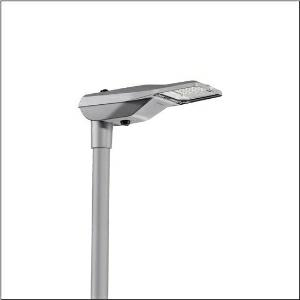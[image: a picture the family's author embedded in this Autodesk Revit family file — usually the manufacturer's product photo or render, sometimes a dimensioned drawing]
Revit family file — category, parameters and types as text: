
# Revit family: streetlight_sl_21_micro___p0_5a_5xe1v33t08db_2423
name_source: partatom
category: Lighting Fixtures
units: mm (PartAtom-declared; Revit-internal decimal feet)

## family parameters
Cut with Voids When Loaded = No
Host = Face
Light Source = No
Part Type = Normal
Room Calculation Point = No
Round Connector Dimension = Use Diameter
Shared = No

## types (1)
- --- (1 x LED, 4940 lm, 39.1 W, 3000K)
    Apparent Load = 39 VA
    CIE Flux Codes = 37 73 96 100 100
    Color Rendering = 70
    Color Temperature = 3000K
    Default Elevation = 1800 mm
    Description = Streetlight SL 21 micro, mast luminaire, primary light control with lens, of PMMA, primary optical cover: cover, of toughened safety glass, transparent, light distribution: P0.5a, light emission: direct distribution, primary light characteristic: asymmetric, installation type: post-top, side-entry, LED, High Power LED, rated luminous flux: 4.940lm, luminous efficacy: 126lm/W, light colour: 730, colour temperature: 3000K, control gear: D4i, control: pre-setting: logarithmic dimming characteristic, flexible luminous flux parameterisation, time-dependent luminous flux control, constant luminous flux control, overheat protection, mains connection: 220..240V, AC, 50/60Hz, start of lifetime: 39W, end of service life: 41W, reduction: 18W, luminaire housing, of diecast aluminium, powder-coated, SITECO metallic grey (DB 702S), corrosivity category C5 high according to DIN EN ISO 12944, multi-level sealing system, sealing non-destructively replaceable, inclination adjustable: 0°, 5°, 10°, 15°, please order mast flange separately, length: 528mm, width: 235mm, height: 110mm, mast flange for spigot size: 42mm (side-entry): 5XC10008XM4, 60/48mm (side-entry/post-top): 5XC10108XM2, 76/60mm (side-entry/post-top): 5XC10108XM1, Smart Interface below and above, protection rating (complete): IP66, insulation class (complete): insulation class II (safety insulation), certification: CE, ENEC, ENEC+, VDE, impact resistance: IK10, permissible operating ambient temperature for outdoor applications: -40..+50°C, standard-compliant lighting for roads and squares, packaging unit: 1 piece

Light Distribution: P0.5a
    Height = 110 mm
    Lamp = 1 x LED
    Lamp Light Flux = 4940 lm
    Lamp Power = 39.1 W
    Lamp count = 1
    Length = 528 mm
    Luminous efficacy = 126 lm/W
    Manufacturer = Siteco
    ModVariant = No
    Model = 5XE1V33T08DB
    Number of Poles = 1
    OnlyDefault = Yes
    Power Factor = 1
    Product Name = Streetlight SL 21 micro | P0.5a
    Product group = mast luminaire | pylon top
    ProductGroupID = 6100
    Protection Class = Protection class II
    Protection Degree = IP 66
    RLX_Detail_Level = 1
    RLX_Emergency_Light_Flux = 0 lm
    RLX_Emergency_Type = 0
    RLX_Emergency_Type_DB = No
    RlxData = <blob elided: 97569 chars, md5=036fe14c>
    Socket = socket
    Standby Power = 0 W
    System Light Flux = 4940 lm
    System Power = 39 W
    Type Comments = factory setting: luminous flux: 100 % | dim-lin: 254 | 765 mA
    Type Image = l_1007239.jpg
    URL = http://relux.com
    VarID = @adj_077807
    Voltage = 0 V
    Weight = 0.00 kg
    Width = 235 mm

## geometry (parser evidence)
native form markers: Blend x4, Sweep x9
no freeform markers — native parametric forms only
